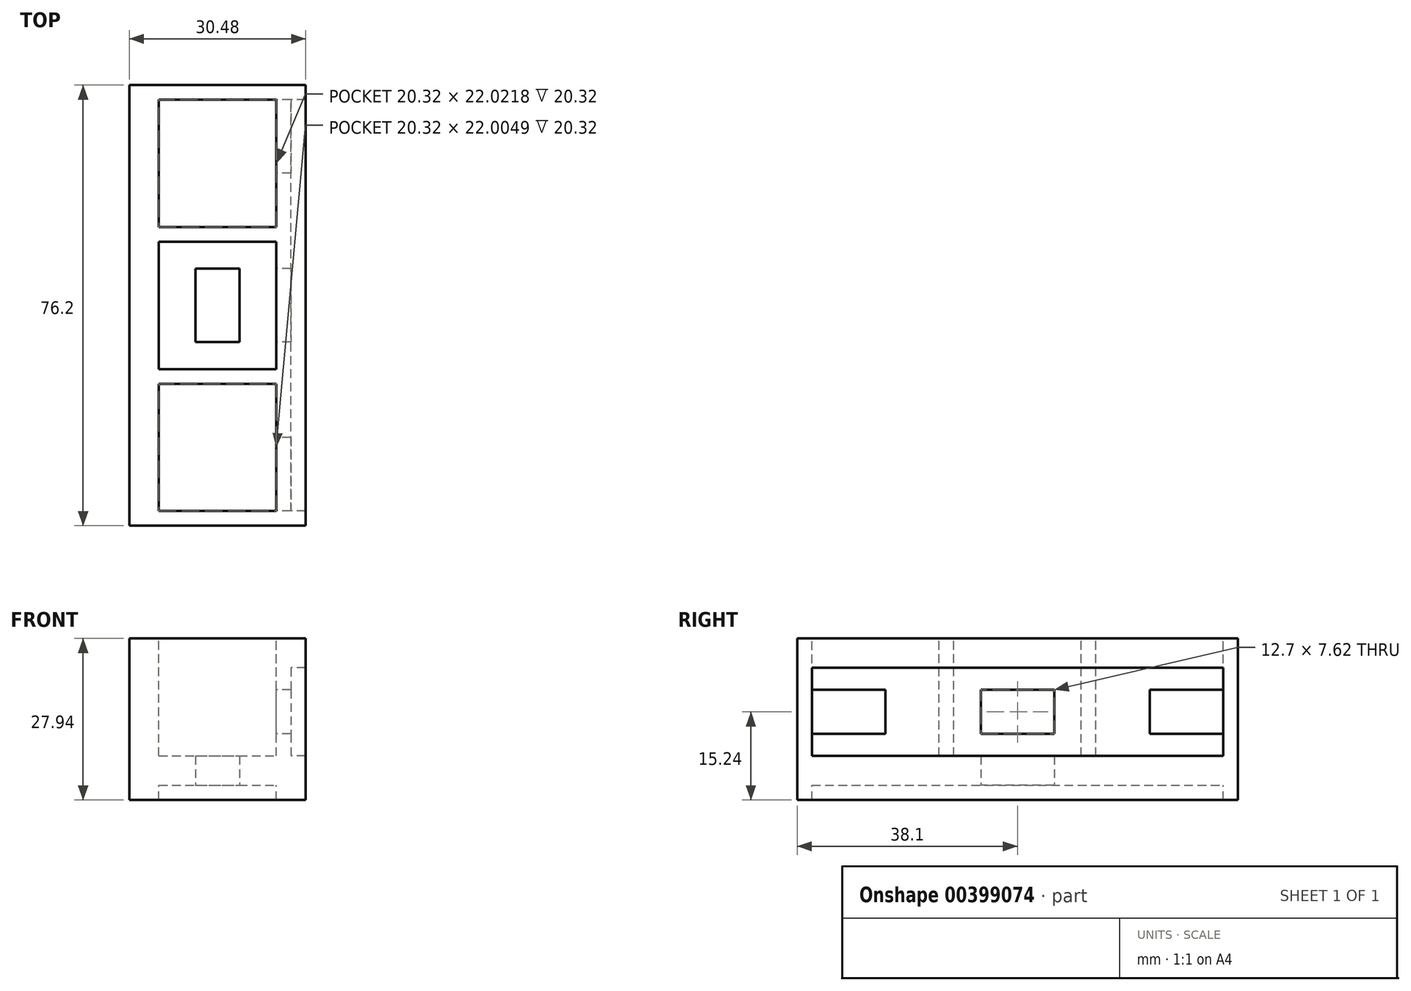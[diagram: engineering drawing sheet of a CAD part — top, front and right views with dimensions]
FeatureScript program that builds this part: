
annotation { "Feature Type Name" : "Feature", "Feature Type Description" : "" }
export const myFeature = defineFeature(function(context is Context, id is Id, definition is map)
    precondition{}
    {
        {
            var Q0;
            Q0=qCreatedBy(makeId("Front.planeOp"),FACE);
            var sketch = newSketch(context, id + "F0", { "sketchPlane" : qUnion([Q0])});
            skLineSegment(sketch, "E0.bottom", {"start": v(0, 0) * mm, "end": v(25.4, 0) * mm});
            skLineSegment(sketch, "E0.top", {"start": v(0, 25.4) * mm, "end": v(25.4, 25.4) * mm});
            skLineSegment(sketch, "E0.left", {"start": v(0, 0) * mm, "end": v(0, 25.4) * mm});
            skLineSegment(sketch, "E0.right", {"start": v(25.4, 0) * mm, "end": v(25.4, 25.4) * mm});
            skSolve(sketch);
        }
        {
            var Q0;
            Q0=makeQuery(id+"F0.imprint","IMPRINT",FACE,{"disambiguationData":[TD([[makeQuery(id+"F0.imprint","IMPRINT",EDGE,{"derivedFrom":sQuery(id+"F0.wireOp",EDGE,"E0.bottom")}),1.0]])]});
            extrude(context, id + "F1", {"entities" : qUnion([Q0]), "depth" : 76.2 * mm});
        }
        {
            var Q0;
            Q0=makeQuery(id+"F1.opExtrude","SWEPT_FACE",FACE,{"disambiguationData":[OSD([sQuery(id+"F0.wireOp",EDGE,"E0.left")])]});
            var sketch = newSketch(context, id + "F2", { "sketchPlane" : qUnion([Q0])});
            skLineSegment(sketch, "E1.bottom", {"start": v(5.08, 16.51) * mm, "end": v(10.16, 16.51) * mm});
            skLineSegment(sketch, "E1.top", {"start": v(5.08, 8.9) * mm, "end": v(10.16, 8.9) * mm});
            skLineSegment(sketch, "E1.left", {"start": v(5.08, 16.51) * mm, "end": v(5.08, 8.9) * mm});
            skLineSegment(sketch, "E1.right", {"start": v(10.16, 16.51) * mm, "end": v(10.16, 8.9) * mm});
            skLineSegment(sketch, "E2.bottom", {"start": v(35.56, 16.51) * mm, "end": v(40.64, 16.51) * mm});
            skLineSegment(sketch, "E2.top", {"start": v(35.56, 8.9) * mm, "end": v(40.64, 8.9) * mm});
            skLineSegment(sketch, "E2.left", {"start": v(35.56, 16.51) * mm, "end": v(35.56, 8.89) * mm});
            skLineSegment(sketch, "E2.right", {"start": v(40.64, 16.51) * mm, "end": v(40.64, 8.9) * mm});
            skLineSegment(sketch, "E3.bottom", {"start": v(66.04, 16.51) * mm, "end": v(71.12, 16.51) * mm});
            skLineSegment(sketch, "E3.top", {"start": v(66.04, 8.89) * mm, "end": v(71.12, 8.9) * mm});
            skLineSegment(sketch, "E3.left", {"start": v(66.04, 16.51) * mm, "end": v(66.04, 8.89) * mm});
            skLineSegment(sketch, "E3.right", {"start": v(71.12, 16.51) * mm, "end": v(71.12, 8.89) * mm});
            skSolve(sketch);
        }
        {
            var Q0;
            Q0=makeQuery(id+"F2.imprint","IMPRINT",FACE,{"disambiguationData":[TD([[makeQuery(id+"F2.imprint","IMPRINT",EDGE,{"derivedFrom":sQuery(id+"F2.wireOp",EDGE,"E1.bottom")}),-1.0]])]});
            var Q1;
            Q1=makeQuery(id+"F2.imprint","IMPRINT",FACE,{"disambiguationData":[TD([[makeQuery(id+"F2.imprint","IMPRINT",EDGE,{"derivedFrom":sQuery(id+"F2.wireOp",EDGE,"E2.bottom")}),-1.0]])]});
            var Q2;
            Q2=makeQuery(id+"F2.imprint","IMPRINT",FACE,{"disambiguationData":[TD([[makeQuery(id+"F2.imprint","IMPRINT",EDGE,{"derivedFrom":sQuery(id+"F2.wireOp",EDGE,"E3.bottom")}),-1.0]])]});
            extrude(context, id + "F3", {"entities" : qUnion([Q0, Q1, Q2]), "operationType" : NewBodyOperationType.REMOVE, "oppositeDirection" : true, "depth" : 25.4 * mm});
        }
        {
            var Q0;
            Q0=makeQuery(id+"F1.opExtrude","SWEPT_FACE",FACE,{"disambiguationData":[OSD([sQuery(id+"F0.wireOp",EDGE,"E0.left")])]});
            var sketch = newSketch(context, id + "F4", { "sketchPlane" : qUnion([Q0])});
            skLineSegment(sketch, "E4.bottom", {"start": v(0, 25.4) * mm, "end": v(76.2, 25.4) * mm});
            skLineSegment(sketch, "E4.top", {"start": v(0, 0) * mm, "end": v(76.2, 0) * mm});
            skLineSegment(sketch, "E4.left", {"start": v(0, 25.4) * mm, "end": v(0, 0) * mm});
            skLineSegment(sketch, "E4.right", {"start": v(76.2, 25.4) * mm, "end": v(76.2, 0) * mm});
            skLineSegment(sketch, "E5.bottom", {"start": v(2.54, 20.32) * mm, "end": v(73.66, 20.32) * mm});
            skLineSegment(sketch, "E5.top", {"start": v(2.54, 5.08) * mm, "end": v(73.66, 5.08) * mm});
            skLineSegment(sketch, "E5.left", {"start": v(2.54, 20.32) * mm, "end": v(2.54, 5.08) * mm});
            skLineSegment(sketch, "E5.right", {"start": v(73.66, 20.32) * mm, "end": v(73.66, 5.08) * mm});
            skSolve(sketch);
        }
        {
            var Q0;
            Q0=makeQuery(id+"F4.imprint","IMPRINT",FACE,{"disambiguationData":[TD([[makeQuery(id+"F4.imprint","IMPRINT",EDGE,{"derivedFrom":sQuery(id+"F4.wireOp",EDGE,"E4.bottom")}),1.0]])]});
            extrude(context, id + "F5", {"entities" : qUnion([Q0]), "operationType" : NewBodyOperationType.ADD, "depth" : 2.54 * mm});
        }
        {
            var Q0;
            Q0=makeQuery(id+"F1.opExtrude","SWEPT_FACE",FACE,{"disambiguationData":[OSD([sQuery(id+"F0.wireOp",EDGE,"E0.right")])]});
            var sketch = newSketch(context, id + "F6", { "sketchPlane" : qUnion([Q0])});
            skLineSegment(sketch, "E6.bottom", {"start": v(-76.2, 25.4) * mm, "end": v(0, 25.4) * mm});
            skLineSegment(sketch, "E6.top", {"start": v(-76.2, 0) * mm, "end": v(0, 0) * mm});
            skLineSegment(sketch, "E6.left", {"start": v(-76.2, 25.4) * mm, "end": v(-76.2, 0) * mm});
            skLineSegment(sketch, "E6.right", {"start": v(0, 25.4) * mm, "end": v(0, 0) * mm});
            skLineSegment(sketch, "E7.bottom", {"start": v(-73.66, 20.32) * mm, "end": v(-2.54, 20.32) * mm});
            skLineSegment(sketch, "E7.top", {"start": v(-73.66, 5.08) * mm, "end": v(-2.54, 5.08) * mm});
            skLineSegment(sketch, "E7.left", {"start": v(-73.66, 20.32) * mm, "end": v(-73.66, 5.08) * mm});
            skLineSegment(sketch, "E7.right", {"start": v(-2.54, 20.32) * mm, "end": v(-2.54, 5.08) * mm});
            skSolve(sketch);
        }
        {
            var Q0;
            Q0=makeQuery(id+"F6.imprint","IMPRINT",FACE,{"disambiguationData":[TD([[makeQuery(id+"F6.imprint","IMPRINT",EDGE,{"derivedFrom":sQuery(id+"F6.wireOp",EDGE,"E6.bottom")}),-1.0]])]});
            extrude(context, id + "F7", {"entities" : qUnion([Q0]), "operationType" : NewBodyOperationType.ADD, "depth" : 2.54 * mm});
        }
        {
            var Q0;
            Q0=makeQuery(id+"F1.opExtrude","SWEPT_FACE",FACE,{"disambiguationData":[OSD([sQuery(id+"F0.wireOp",EDGE,"E0.left")])]});
            var sketch = newSketch(context, id + "F8", { "sketchPlane" : qUnion([Q0])});
            skLineSegment(sketch, "E8.bottom", {"start": v(71.12, 16.51) * mm, "end": v(73.66, 16.51) * mm});
            skLineSegment(sketch, "E8.top", {"start": v(71.12, 8.9) * mm, "end": v(73.66, 8.9) * mm});
            skLineSegment(sketch, "E8.left", {"start": v(71.12, 16.51) * mm, "end": v(71.12, 8.9) * mm});
            skLineSegment(sketch, "E8.right", {"start": v(73.66, 16.51) * mm, "end": v(73.66, 8.9) * mm});
            skLineSegment(sketch, "E9.bottom", {"start": v(66.04, 16.51) * mm, "end": v(60.96, 16.51) * mm});
            skLineSegment(sketch, "E9.top", {"start": v(66.04, 8.89) * mm, "end": v(60.96, 8.89) * mm});
            skLineSegment(sketch, "E9.left", {"start": v(66.04, 16.51) * mm, "end": v(66.04, 8.89) * mm});
            skLineSegment(sketch, "E9.right", {"start": v(60.96, 16.51) * mm, "end": v(60.96, 8.89) * mm});
            skLineSegment(sketch, "E10.bottom", {"start": v(5.08, 16.51) * mm, "end": v(2.54, 16.51) * mm});
            skLineSegment(sketch, "E10.top", {"start": v(5.08, 8.9) * mm, "end": v(2.54, 8.9) * mm});
            skLineSegment(sketch, "E10.left", {"start": v(5.08, 16.51) * mm, "end": v(5.08, 8.9) * mm});
            skLineSegment(sketch, "E10.right", {"start": v(2.54, 16.51) * mm, "end": v(2.54, 8.9) * mm});
            skLineSegment(sketch, "E11.bottom", {"start": v(10.16, 16.51) * mm, "end": v(15.24, 16.51) * mm});
            skLineSegment(sketch, "E11.top", {"start": v(10.16, 8.9) * mm, "end": v(15.24, 8.9) * mm});
            skLineSegment(sketch, "E11.left", {"start": v(10.16, 16.51) * mm, "end": v(10.16, 8.9) * mm});
            skLineSegment(sketch, "E11.right", {"start": v(15.24, 16.51) * mm, "end": v(15.24, 8.9) * mm});
            skLineSegment(sketch, "E12.bottom", {"start": v(35.56, 16.51) * mm, "end": v(31.75, 16.51) * mm});
            skLineSegment(sketch, "E12.top", {"start": v(35.56, 8.89) * mm, "end": v(31.75, 8.89) * mm});
            skLineSegment(sketch, "E12.left", {"start": v(35.56, 16.51) * mm, "end": v(35.56, 8.89) * mm});
            skLineSegment(sketch, "E12.right", {"start": v(31.75, 16.51) * mm, "end": v(31.75, 8.89) * mm});
            skLineSegment(sketch, "E13.bottom", {"start": v(40.64, 16.51) * mm, "end": v(44.45, 16.51) * mm});
            skLineSegment(sketch, "E13.top", {"start": v(40.64, 8.89) * mm, "end": v(44.45, 8.89) * mm});
            skLineSegment(sketch, "E13.left", {"start": v(40.64, 16.51) * mm, "end": v(40.64, 8.89) * mm});
            skLineSegment(sketch, "E13.right", {"start": v(44.45, 16.51) * mm, "end": v(44.45, 8.89) * mm});
            skSolve(sketch);
        }
        {
            var Q0;
            Q0=makeQuery(id+"F8.imprint","IMPRINT",FACE,{"disambiguationData":[TD([[makeQuery(id+"F8.imprint","IMPRINT",EDGE,{"derivedFrom":sQuery(id+"F8.wireOp",EDGE,"E11.bottom")}),-1.0]])]});
            var Q1;
            Q1=makeQuery(id+"F8.imprint","IMPRINT",FACE,{"disambiguationData":[TD([[makeQuery(id+"F8.imprint","IMPRINT",EDGE,{"derivedFrom":sQuery(id+"F8.wireOp",EDGE,"E10.bottom")}),1.0]])]});
            var Q2;
            Q2=makeQuery(id+"F8.imprint","IMPRINT",FACE,{"disambiguationData":[TD([[makeQuery(id+"F8.imprint","IMPRINT",EDGE,{"derivedFrom":sQuery(id+"F8.wireOp",EDGE,"E12.bottom")}),1.0]])]});
            var Q3;
            Q3=makeQuery(id+"F8.imprint","IMPRINT",FACE,{"disambiguationData":[TD([[makeQuery(id+"F8.imprint","IMPRINT",EDGE,{"derivedFrom":sQuery(id+"F8.wireOp",EDGE,"E13.bottom")}),-1.0]])]});
            var Q4;
            Q4=makeQuery(id+"F8.imprint","IMPRINT",FACE,{"disambiguationData":[TD([[makeQuery(id+"F8.imprint","IMPRINT",EDGE,{"derivedFrom":sQuery(id+"F8.wireOp",EDGE,"E9.bottom")}),1.0]])]});
            var Q5;
            Q5=makeQuery(id+"F8.imprint","IMPRINT",FACE,{"disambiguationData":[TD([[makeQuery(id+"F8.imprint","IMPRINT",EDGE,{"derivedFrom":sQuery(id+"F8.wireOp",EDGE,"E8.bottom")}),-1.0]])]});
            extrude(context, id + "F9", {"entities" : qUnion([Q0, Q1, Q2, Q3, Q4, Q5]), "operationType" : NewBodyOperationType.REMOVE, "oppositeDirection" : true, "depth" : 25.4 * mm});
        }
        {
            var Q0;
            Q0=makeQuery(id+"F7.boolean.opBoolean","MERGE",FACE,{"derivedFrom":[makeQuery(id+"F5.boolean.opBoolean","MERGE",FACE,{"derivedFrom":[makeQuery(id+"F1.opExtrude","SWEPT_FACE",FACE,{"disambiguationData":[OSD([sQuery(id+"F0.wireOp",EDGE,"E0.bottom")])]}),makeQuery(id+"F5.opExtrude","SWEPT_FACE",FACE,{"disambiguationData":[OSD([sQuery(id+"F4.wireOp",EDGE,"E4.top")])]})]}),makeQuery(id+"F7.opExtrude","SWEPT_FACE",FACE,{"disambiguationData":[OSD([sQuery(id+"F6.wireOp",EDGE,"E6.top")])]})]});
            var sketch = newSketch(context, id + "F10", { "sketchPlane" : qUnion([Q0])});
            skLineSegment(sketch, "E14.bottom", {"start": v(0, 2.54) * mm, "end": v(25.4, 2.54) * mm});
            skLineSegment(sketch, "E14.top", {"start": v(0, 73.66) * mm, "end": v(25.4, 73.66) * mm});
            skLineSegment(sketch, "E14.left", {"start": v(0, 2.54) * mm, "end": v(0, 73.66) * mm});
            skLineSegment(sketch, "E14.right", {"start": v(25.4, 2.54) * mm, "end": v(25.4, 73.66) * mm});
            skLineSegment(sketch, "E15.bottom", {"start": v(8.89, 2.54) * mm, "end": v(16.51, 2.54) * mm});
            skLineSegment(sketch, "E15.top", {"start": v(8.89, 15.24) * mm, "end": v(16.51, 15.24) * mm});
            skLineSegment(sketch, "E15.left", {"start": v(8.89, 2.54) * mm, "end": v(8.89, 15.24) * mm});
            skLineSegment(sketch, "E15.right", {"start": v(16.51, 2.54) * mm, "end": v(16.51, 15.24) * mm});
            skLineSegment(sketch, "E16.bottom", {"start": v(8.9, 31.75) * mm, "end": v(16.51, 31.75) * mm});
            skLineSegment(sketch, "E16.top", {"start": v(8.89, 44.45) * mm, "end": v(16.5, 44.45) * mm});
            skLineSegment(sketch, "E16.left", {"start": v(8.9, 31.75) * mm, "end": v(8.89, 44.45) * mm});
            skLineSegment(sketch, "E16.right", {"start": v(16.51, 31.75) * mm, "end": v(16.5, 44.45) * mm});
            skLineSegment(sketch, "E17.bottom", {"start": v(8.89, 73.66) * mm, "end": v(16.5, 73.66) * mm});
            skLineSegment(sketch, "E17.top", {"start": v(8.89, 60.96) * mm, "end": v(16.5, 60.96) * mm});
            skLineSegment(sketch, "E17.left", {"start": v(8.89, 73.66) * mm, "end": v(8.89, 60.96) * mm});
            skLineSegment(sketch, "E17.right", {"start": v(16.5, 73.66) * mm, "end": v(16.5, 60.96) * mm});
            skSolve(sketch);
        }
        {
            var Q0;
            Q0=makeQuery(id+"F10.imprint","IMPRINT",FACE,{"disambiguationData":[TD([[makeQuery(id+"F10.imprint","IMPRINT",EDGE,{"derivedFrom":sQuery(id+"F10.wireOp",EDGE,"E15.bottom")}),1.0]])]});
            var Q1;
            Q1=makeQuery(id+"F10.imprint","IMPRINT",FACE,{"disambiguationData":[TD([[makeQuery(id+"F10.imprint","IMPRINT",EDGE,{"derivedFrom":sQuery(id+"F10.wireOp",EDGE,"E16.bottom")}),1.0]])]});
            var Q2;
            Q2=makeQuery(id+"F10.imprint","IMPRINT",FACE,{"disambiguationData":[TD([[makeQuery(id+"F10.imprint","IMPRINT",EDGE,{"derivedFrom":sQuery(id+"F10.wireOp",EDGE,"E17.bottom")}),-1.0]])]});
            extrude(context, id + "F11", {"entities" : qUnion([Q0, Q1, Q2]), "operationType" : NewBodyOperationType.REMOVE, "oppositeDirection" : true, "depth" : 25.4 * mm});
        }
        {
            var Q0;
            Q0=makeQuery(id+"F7.boolean.opBoolean","MERGE",FACE,{"derivedFrom":[makeQuery(id+"F5.boolean.opBoolean","MERGE",FACE,{"derivedFrom":[makeQuery(id+"F1.opExtrude","SWEPT_FACE",FACE,{"disambiguationData":[OSD([sQuery(id+"F0.wireOp",EDGE,"E0.bottom")])]}),makeQuery(id+"F5.opExtrude","SWEPT_FACE",FACE,{"disambiguationData":[OSD([sQuery(id+"F4.wireOp",EDGE,"E4.top")])]})]}),makeQuery(id+"F7.opExtrude","SWEPT_FACE",FACE,{"disambiguationData":[OSD([sQuery(id+"F6.wireOp",EDGE,"E6.top")])]})]});
            var sketch = newSketch(context, id + "F12", { "sketchPlane" : qUnion([Q0])});
            skLineSegment(sketch, "E18.bottom", {"start": v(0, 73.66) * mm, "end": v(22.86, 73.66) * mm});
            skLineSegment(sketch, "E19.bottom", {"start": v(0, 73.66) * mm, "end": v(25.4, 73.66) * mm});
            skLineSegment(sketch, "E19.top", {"start": v(0, 2.54) * mm, "end": v(25.4, 2.54) * mm});
            skLineSegment(sketch, "E19.left", {"start": v(0, 73.66) * mm, "end": v(0, 2.54) * mm});
            skLineSegment(sketch, "E19.right", {"start": v(25.4, 73.66) * mm, "end": v(25.4, 2.54) * mm});
            skLineSegment(sketch, "E20.bottom", {"start": v(2.54, 73.66) * mm, "end": v(22.86, 73.66) * mm});
            skLineSegment(sketch, "E20.top", {"start": v(2.54, 2.54) * mm, "end": v(22.86, 2.54) * mm});
            skLineSegment(sketch, "E20.left", {"start": v(2.54, 73.66) * mm, "end": v(2.54, 2.54) * mm});
            skLineSegment(sketch, "E20.right", {"start": v(22.86, 73.66) * mm, "end": v(22.86, 2.54) * mm});
            skLineSegment(sketch, "E21.top", {"start": v(0, 76.2) * mm, "end": v(25.4, 76.2) * mm});
            skLineSegment(sketch, "E21.left", {"start": v(0, 73.66) * mm, "end": v(0, 76.2) * mm});
            skLineSegment(sketch, "E21.right", {"start": v(25.4, 73.66) * mm, "end": v(25.4, 76.2) * mm});
            skLineSegment(sketch, "E22.top", {"start": v(0, 0) * mm, "end": v(25.4, 0) * mm});
            skLineSegment(sketch, "E22.left", {"start": v(0, 2.54) * mm, "end": v(0, 0) * mm});
            skLineSegment(sketch, "E22.right", {"start": v(25.4, 2.54) * mm, "end": v(25.4, 0) * mm});
            skSolve(sketch);
        }
        {
            var Q0;
            Q0=makeQuery(id+"F12.imprint","IMPRINT",FACE,{"disambiguationData":[TD([[makeQuery(id+"F12.imprint","IMPRINT",EDGE,{"derivedFrom":sQuery(id+"F12.wireOp",EDGE,"E21.top")}),-1.0]])]});
            var Q1;
            {var subQ0=sQuery(id+"F12.wireOp",EDGE,"E19.left");Q1=makeQuery(id+"F12.imprint","IMPRINT",FACE,{"disambiguationData":[TD([[makeQuery(id+"F12.imprint","IMPRINT",EDGE,{"derivedFrom":subQ0}),1.0]])]});}
            var Q2;
            {var subQ0=sQuery(id+"F12.wireOp",EDGE,"E19.right");Q2=makeQuery(id+"F12.imprint","IMPRINT",FACE,{"disambiguationData":[TD([[makeQuery(id+"F12.imprint","IMPRINT",EDGE,{"derivedFrom":subQ0}),-1.0]])]});}
            var Q3;
            Q3=makeQuery(id+"F12.imprint","IMPRINT",FACE,{"disambiguationData":[TD([[makeQuery(id+"F12.imprint","IMPRINT",EDGE,{"derivedFrom":sQuery(id+"F12.wireOp",EDGE,"E22.top")}),1.0]])]});
            extrude(context, id + "F13", {"entities" : qUnion([Q0, Q1, Q2, Q3]), "operationType" : NewBodyOperationType.ADD, "depth" : 2.54 * mm});
        }
        {
            var Q0;
            Q0=makeQuery(id+"F1.opExtrude","SWEPT_FACE",FACE,{"disambiguationData":[OSD([sQuery(id+"F0.wireOp",EDGE,"E0.left")])]});
            var sketch = newSketch(context, id + "F14", { "sketchPlane" : qUnion([Q0])});
            skLineSegment(sketch, "E23.bottom", {"start": v(2.54, 20.32) * mm, "end": v(73.66, 20.32) * mm});
            skLineSegment(sketch, "E23.top", {"start": v(2.54, 5.08) * mm, "end": v(73.66, 5.08) * mm});
            skLineSegment(sketch, "E23.left", {"start": v(2.54, 20.32) * mm, "end": v(2.54, 5.08) * mm});
            skLineSegment(sketch, "E23.right", {"start": v(73.66, 20.32) * mm, "end": v(73.66, 5.08) * mm});
            skSolve(sketch);
        }
        {
            var Q0;
            Q0 = qSketchRegion(id + "F14", true);
            extrude(context, id + "F15", {"entities" : qUnion([Q0]), "operationType" : NewBodyOperationType.ADD, "depth" : 2.54 * mm});
        }
        {
            var Q0;
            Q0=makeQuery(id+"F15.boolean.opBoolean","SPLIT",FACE,{"disambiguationData":[TD([makeQuery(id+"F3.boolean.opBoolean","COPY",FACE,{"derivedFrom":makeQuery(id+"F3.opExtrude","SWEPT_FACE",FACE,{"disambiguationData":[OSD([sQuery(id+"F2.wireOp",EDGE,"E2.bottom")])]})})])],"derivedFrom":makeQuery(id+"F15.opExtrude","CAP_FACE",FACE,{"disambiguationData":[OSD([sQuery(id+"F14.wireOp",EDGE,"E23.bottom"),sQuery(id+"F14.wireOp",EDGE,"E23.top"),sQuery(id+"F14.wireOp",EDGE,"E23.left"),sQuery(id+"F14.wireOp",EDGE,"E23.right")])],"isStart":true})});
            var sketch = newSketch(context, id + "F16", { "sketchPlane" : qUnion([Q0])});
            skLineSegment(sketch, "E24.bottom", {"start": v(-44.45, 16.51) * mm, "end": v(-31.75, 16.51) * mm});
            skLineSegment(sketch, "E24.top", {"start": v(-44.45, 8.89) * mm, "end": v(-31.75, 8.89) * mm});
            skLineSegment(sketch, "E24.left", {"start": v(-44.45, 16.51) * mm, "end": v(-44.45, 8.89) * mm});
            skLineSegment(sketch, "E24.right", {"start": v(-31.75, 16.51) * mm, "end": v(-31.75, 8.89) * mm});
            skSolve(sketch);
        }
        {
            var Q0;
            Q0 = qSketchRegion(id + "F16", true);
            extrude(context, id + "F17", {"entities" : qUnion([Q0]), "operationType" : NewBodyOperationType.ADD, "depth" : 8.9 * mm});
        }
        {
            var Q0;
            Q0=makeQuery(id+"F15.boolean.opBoolean","SPLIT",FACE,{"disambiguationData":[TD([makeQuery(id+"F3.boolean.opBoolean","COPY",FACE,{"derivedFrom":makeQuery(id+"F3.opExtrude","SWEPT_FACE",FACE,{"disambiguationData":[OSD([sQuery(id+"F2.wireOp",EDGE,"E3.bottom")])]})})])],"derivedFrom":makeQuery(id+"F15.opExtrude","CAP_FACE",FACE,{"disambiguationData":[OSD([sQuery(id+"F14.wireOp",EDGE,"E23.bottom"),sQuery(id+"F14.wireOp",EDGE,"E23.top"),sQuery(id+"F14.wireOp",EDGE,"E23.left"),sQuery(id+"F14.wireOp",EDGE,"E23.right")])],"isStart":true})});
            var sketch = newSketch(context, id + "F18", { "sketchPlane" : qUnion([Q0])});
            skLineSegment(sketch, "E25.bottom", {"start": v(-73.66, 16.51) * mm, "end": v(-60.96, 16.51) * mm});
            skLineSegment(sketch, "E25.top", {"start": v(-73.66, 8.89) * mm, "end": v(-60.96, 8.89) * mm});
            skLineSegment(sketch, "E25.left", {"start": v(-73.66, 16.51) * mm, "end": v(-73.66, 8.89) * mm});
            skLineSegment(sketch, "E25.right", {"start": v(-60.96, 16.51) * mm, "end": v(-60.96, 8.89) * mm});
            skSolve(sketch);
        }
        {
            var Q0;
            Q0=makeQuery(id+"F18.imprint","IMPRINT",FACE,{"disambiguationData":[TD([[makeQuery(id+"F18.imprint","IMPRINT",EDGE,{"derivedFrom":sQuery(id+"F18.wireOp",EDGE,"E25.bottom")}),1.0]])]});
            extrude(context, id + "F19", {"entities" : qUnion([Q0]), "operationType" : NewBodyOperationType.ADD, "depth" : 8.9 * mm});
        }
        {
            var Q0;
            Q0=makeQuery(id+"F15.boolean.opBoolean","SPLIT",FACE,{"disambiguationData":[TD([makeQuery(id+"F3.boolean.opBoolean","COPY",FACE,{"derivedFrom":makeQuery(id+"F3.opExtrude","SWEPT_FACE",FACE,{"disambiguationData":[OSD([sQuery(id+"F2.wireOp",EDGE,"E1.bottom")])]})})])],"derivedFrom":makeQuery(id+"F15.opExtrude","CAP_FACE",FACE,{"disambiguationData":[OSD([sQuery(id+"F14.wireOp",EDGE,"E23.bottom"),sQuery(id+"F14.wireOp",EDGE,"E23.top"),sQuery(id+"F14.wireOp",EDGE,"E23.left"),sQuery(id+"F14.wireOp",EDGE,"E23.right")])],"isStart":true})});
            var sketch = newSketch(context, id + "F20", { "sketchPlane" : qUnion([Q0])});
            skLineSegment(sketch, "E26.bottom", {"start": v(-15.24, 16.51) * mm, "end": v(-2.54, 16.51) * mm});
            skLineSegment(sketch, "E26.top", {"start": v(-15.24, 8.9) * mm, "end": v(-2.54, 8.9) * mm});
            skLineSegment(sketch, "E26.left", {"start": v(-15.24, 16.51) * mm, "end": v(-15.24, 8.9) * mm});
            skLineSegment(sketch, "E26.right", {"start": v(-2.54, 16.51) * mm, "end": v(-2.54, 8.9) * mm});
            skSolve(sketch);
        }
        {
            var Q0;
            Q0=makeQuery(id+"F20.imprint","IMPRINT",FACE,{"disambiguationData":[TD([[makeQuery(id+"F20.imprint","IMPRINT",EDGE,{"derivedFrom":sQuery(id+"F20.wireOp",EDGE,"E26.bottom")}),1.0]])]});
            extrude(context, id + "F21", {"entities" : qUnion([Q0]), "operationType" : NewBodyOperationType.ADD, "depth" : 8.9 * mm});
        }
        {
            var Q0;
            Q0=makeQuery(id+"F7.boolean.opBoolean","MERGE",FACE,{"derivedFrom":[makeQuery(id+"F5.boolean.opBoolean","MERGE",FACE,{"derivedFrom":[makeQuery(id+"F1.opExtrude","SWEPT_FACE",FACE,{"disambiguationData":[OSD([sQuery(id+"F0.wireOp",EDGE,"E0.top")])]}),makeQuery(id+"F5.opExtrude","SWEPT_FACE",FACE,{"disambiguationData":[OSD([sQuery(id+"F4.wireOp",EDGE,"E4.bottom")])]})]}),makeQuery(id+"F7.opExtrude","SWEPT_FACE",FACE,{"disambiguationData":[OSD([sQuery(id+"F6.wireOp",EDGE,"E6.bottom")])]})]});
            var sketch = newSketch(context, id + "F22", { "sketchPlane" : qUnion([Q0])});
            skLineSegment(sketch, "E27.bottom", {"start": v(0, 0) * mm, "end": v(25.4, 0) * mm});
            skLineSegment(sketch, "E27.top", {"start": v(0, -76.2) * mm, "end": v(25.4, -76.2) * mm});
            skLineSegment(sketch, "E27.left", {"start": v(0, -2.54) * mm, "end": v(0, -76.2) * mm});
            skLineSegment(sketch, "E27.right", {"start": v(25.4, -2.54) * mm, "end": v(25.4, -76.2) * mm});
            skLineSegment(sketch, "E28.bottom", {"start": v(2.54, -73.66) * mm, "end": v(22.86, -73.66) * mm});
            skLineSegment(sketch, "E28.top", {"start": v(2.54, -51.66) * mm, "end": v(22.86, -51.66) * mm});
            skLineSegment(sketch, "E28.left", {"start": v(2.54, -73.66) * mm, "end": v(2.54, -51.66) * mm});
            skLineSegment(sketch, "E28.right", {"start": v(22.86, -73.66) * mm, "end": v(22.86, -51.66) * mm});
            skLineSegment(sketch, "E29.bottom", {"start": v(2.54, -27.1) * mm, "end": v(22.86, -27.1) * mm});
            skLineSegment(sketch, "E29.top", {"start": v(2.54, -49.12) * mm, "end": v(22.86, -49.12) * mm});
            skLineSegment(sketch, "E29.left", {"start": v(2.54, -27.1) * mm, "end": v(2.54, -49.12) * mm});
            skLineSegment(sketch, "E29.right", {"start": v(22.86, -27.1) * mm, "end": v(22.86, -49.12) * mm});
            skLineSegment(sketch, "E30.top", {"start": v(0, -2.54) * mm, "end": v(25.4, -2.54) * mm});
            skLineSegment(sketch, "E31.bottom", {"start": v(2.54, -2.54) * mm, "end": v(22.86, -2.54) * mm});
            skLineSegment(sketch, "E31.top", {"start": v(2.54, -24.56) * mm, "end": v(22.86, -24.56) * mm});
            skLineSegment(sketch, "E31.left", {"start": v(2.54, -2.54) * mm, "end": v(2.54, -24.56) * mm});
            skLineSegment(sketch, "E31.right", {"start": v(22.86, -2.54) * mm, "end": v(22.86, -24.56) * mm});
            skSolve(sketch);
        }
        {
            var Q0;
            Q0=makeQuery(id+"F22.imprint","IMPRINT",FACE,{"disambiguationData":[TD([[makeQuery(id+"F22.imprint","IMPRINT",EDGE,{"derivedFrom":sQuery(id+"F22.wireOp",EDGE,"E31.top")}),1.0]])]});
            var Q1;
            Q1=makeQuery(id+"F22.imprint","IMPRINT",FACE,{"disambiguationData":[TD([[makeQuery(id+"F22.imprint","IMPRINT",EDGE,{"derivedFrom":sQuery(id+"F22.wireOp",EDGE,"E29.bottom")}),-1.0]])]});
            var Q2;
            Q2=makeQuery(id+"F22.imprint","IMPRINT",FACE,{"disambiguationData":[TD([[makeQuery(id+"F22.imprint","IMPRINT",EDGE,{"derivedFrom":sQuery(id+"F22.wireOp",EDGE,"E28.top")}),-1.0]])]});
            extrude(context, id + "F23", {"entities" : qUnion([Q0, Q1, Q2]), "operationType" : NewBodyOperationType.REMOVE, "oppositeDirection" : true, "depth" : 20.32 * mm});
        }
        {
            var Q0;
            Q0=makeQuery(id+"F13.opExtrude","SWEPT_FACE",FACE,{"disambiguationData":[OSD([sQuery(id+"F12.wireOp",EDGE,"E19.left"),sQuery(id+"F12.wireOp",EDGE,"E21.left"),sQuery(id+"F12.wireOp",EDGE,"E22.left")])]});
            var sketch = newSketch(context, id + "F24", { "sketchPlane" : qUnion([Q0])});
            skSolve(sketch);
        }
        {
            var Q0;
            {var subQ0=sQuery(id+"F12.wireOp",EDGE,"E21.left");var subQ4=sQuery(id+"F12.wireOp",EDGE,"E22.left");var subQ5=sQuery(id+"F12.wireOp",EDGE,"E19.left");Q0=makeQuery(id+"F24.imprint","IMPRINT",FACE,{"disambiguationData":[TD([[makeQuery(id+"F24.imprint","IMPRINT",EDGE,{"derivedFrom":makeQuery(id+"F13.opExtrude","CAP_EDGE",EDGE,{"disambiguationData":[OSD([subQ5,subQ0,subQ4])],"isStart":false})}),1.0]])]});}
            var sketch = newSketch(context, id + "F25", { "sketchPlane" : qUnion([Q0])});
            skLineSegment(sketch, "E32.bottom", {"start": v(0, 0) * mm, "end": v(76.2, 0) * mm});
            skLineSegment(sketch, "E32.top", {"start": v(0, -2.54) * mm, "end": v(76.2, -2.54) * mm});
            skLineSegment(sketch, "E32.left", {"start": v(0, 0) * mm, "end": v(0, -2.54) * mm});
            skLineSegment(sketch, "E32.right", {"start": v(76.2, 0) * mm, "end": v(76.2, -2.54) * mm});
            skSolve(sketch);
        }
        {
            var Q0;
            Q0 = qSketchRegion(id + "F25", true);
            extrude(context, id + "F26", {"entities" : qUnion([Q0]), "operationType" : NewBodyOperationType.ADD, "depth" : 2.54 * mm});
        }
        {
            var Q0;
            {var subQ3=sQuery(id+"F0.wireOp",EDGE,"E0.bottom");var subQ6=sQuery(id+"F6.wireOp",EDGE,"E6.top");Q0=makeQuery(id+"F13.boolean.opBoolean","SPLIT",FACE,{"disambiguationData":[TD([makeQuery(id+"F13.opExtrude","SWEPT_FACE",FACE,{"disambiguationData":[OSD([sQuery(id+"F12.wireOp",EDGE,"E19.right"),sQuery(id+"F12.wireOp",EDGE,"E21.right"),sQuery(id+"F12.wireOp",EDGE,"E22.right")])]})])],"derivedFrom":makeQuery(id+"F7.boolean.opBoolean","MERGE",FACE,{"derivedFrom":[makeQuery(id+"F5.boolean.opBoolean","MERGE",FACE,{"derivedFrom":[makeQuery(id+"F1.opExtrude","SWEPT_FACE",FACE,{"disambiguationData":[OSD([subQ3])]}),makeQuery(id+"F5.opExtrude","SWEPT_FACE",FACE,{"disambiguationData":[OSD([sQuery(id+"F4.wireOp",EDGE,"E4.top")])]})]}),makeQuery(id+"F7.opExtrude","SWEPT_FACE",FACE,{"disambiguationData":[OSD([subQ6])]})]})});}
            var sketch = newSketch(context, id + "F27", { "sketchPlane" : qUnion([Q0])});
            skLineSegment(sketch, "E33.bottom", {"start": v(25.4, 76.2) * mm, "end": v(27.94, 76.2) * mm});
            skLineSegment(sketch, "E33.top", {"start": v(25.4, 0) * mm, "end": v(27.94, 0) * mm});
            skLineSegment(sketch, "E33.left", {"start": v(25.4, 76.2) * mm, "end": v(25.4, 0) * mm});
            skLineSegment(sketch, "E33.right", {"start": v(27.94, 76.2) * mm, "end": v(27.94, 0) * mm});
            skSolve(sketch);
        }
        {
            var Q0;
            Q0=makeQuery(id+"F27.imprint","IMPRINT",FACE,{"disambiguationData":[TD([[makeQuery(id+"F27.imprint","IMPRINT",EDGE,{"derivedFrom":sQuery(id+"F27.wireOp",EDGE,"E33.bottom")}),-1.0]])]});
            extrude(context, id + "F28", {"entities" : qUnion([Q0]), "operationType" : NewBodyOperationType.ADD, "depth" : 2.54 * mm});
        }
    });
